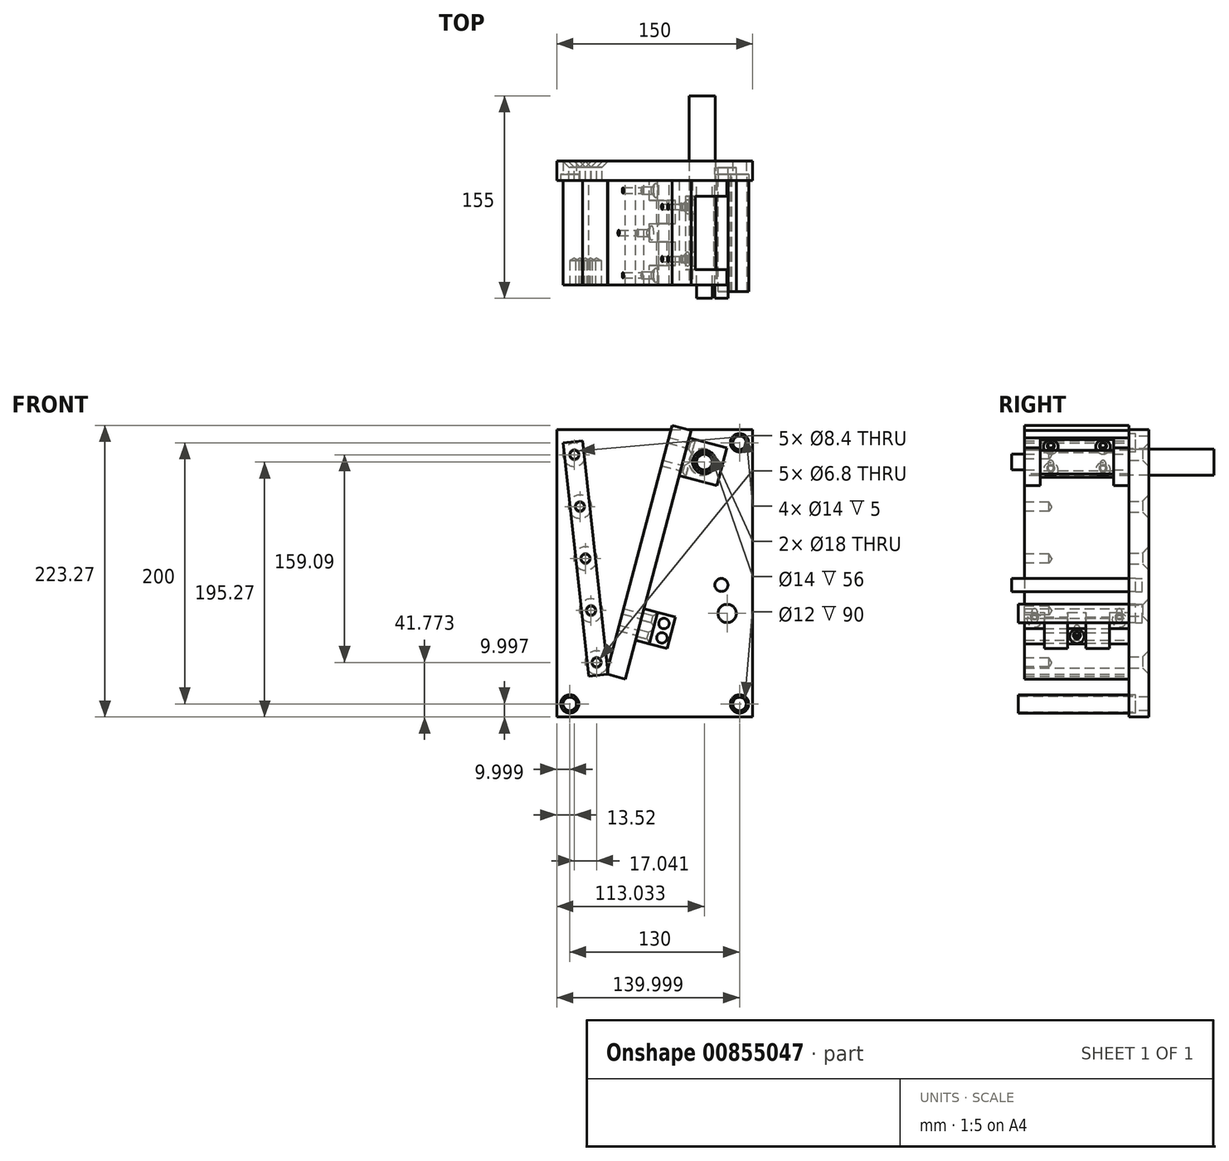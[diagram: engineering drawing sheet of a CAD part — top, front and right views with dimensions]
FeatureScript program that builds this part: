
annotation { "Feature Type Name" : "Feature", "Feature Type Description" : "" }
export const myFeature = defineFeature(function(context is Context, id is Id, definition is map)
    precondition{}
    {
        {
            var Q0;
            Q0=qCreatedBy(makeId("Front.planeOp"),FACE);
            var sketch = newSketch(context, id + "F0", { "sketchPlane" : qUnion([Q0])});
            skLineSegment(sketch, "E0", {"start": v(-17.27, 159) * mm, "end": v(0, 0) * mm});
            skLineSegment(sketch, "E1", {"start": v(0, 0) * mm, "end": v(42, 159) * mm});
            skLineSegment(sketch, "E2", {"start": v(42, 159) * mm, "end": v(142, 159) * mm});
            skLineSegment(sketch, "E3", {"start": v(142, 159) * mm, "end": v(123.08, 24.32) * mm});
            skLineSegment(sketch, "E4", {"start": v(123.08, 24.32) * mm, "end": v(218.62, 60.04) * mm});
            skLineSegment(sketch, "E5", {"start": v(124.98, 37.82) * mm, "end": v(164.87, 64.53) * mm});
            skLineSegment(sketch, "E6", {"start": v(-37.17, 28.68) * mm, "end": v(-37.17, -31.23) * mm, "construction": true});
            skLineSegment(sketch, "E7", {"start": v(-15.81, -31.23) * mm, "end": v(52.07, -31.23) * mm, "construction": true});
            skCircle(sketch, "E8", {"center": v(142, 159) * mm, "radius": 55 * mm});
            skCircle(sketch, "E9", {"center": v(142.6, 159) * mm, "radius": 8 * mm});
            skSolve(sketch);
        }
        {
            var Q0;
            Q0=qCreatedBy(makeId("Front.planeOp"),FACE);
            var sketch = newSketch(context, id + "F1", { "sketchPlane" : qUnion([Q0])});
            skLineSegment(sketch, "E10.bottom", {"start": v(-19.05, 175.35) * mm, "end": v(-33.96, 173.73) * mm});
            skLineSegment(sketch, "E10.top", {"start": v(-0.15, -3.66) * mm, "end": v(-14.52, -5.22) * mm});
            skLineSegment(sketch, "E10.left", {"start": v(-19.05, 175.35) * mm, "end": v(-0.15, 1.34) * mm});
            skLineSegment(sketch, "E10.right", {"start": v(-33.96, 173.73) * mm, "end": v(-14.52, -5.22) * mm});
            skLineSegment(sketch, "E11", {"start": v(-0.15, 1.34) * mm, "end": v(-0.15, -3.66) * mm});
            skLineSegment(sketch, "E12", {"start": v(0.35, 1.34) * mm, "end": v(0.35, -3.66) * mm, "construction": true});
            skSolve(sketch);
        }
        {
            var Q0;
            Q0 = qSketchRegion(id + "F1", true);
            extrude(context, id + "F2", {"entities" : qUnion([Q0]), "depth" : 80 * mm, "offsetDistance" : 25 * mm});
        }
        {
            var Q0;
            Q0=qCreatedBy(makeId("Front.planeOp"),FACE);
            var sketch = newSketch(context, id + "F3", { "sketchPlane" : qUnion([Q0])});
            skLineSegment(sketch, "E13.bottom", {"start": v(0.35, -3.66) * mm, "end": v(13.62, -7.16) * mm});
            skLineSegment(sketch, "E13.top", {"start": v(49.4, 187) * mm, "end": v(63.91, 183.17) * mm});
            skLineSegment(sketch, "E13.left", {"start": v(49.4, 187) * mm, "end": v(0.35, 1.34) * mm});
            skLineSegment(sketch, "E13.right", {"start": v(63.91, 183.17) * mm, "end": v(13.62, -7.16) * mm});
            skLineSegment(sketch, "E14", {"start": v(0.35, -3.66) * mm, "end": v(0.35, 1.34) * mm});
            skPoint(sketch, "E15", {"position": v(57.52, 159) * mm});
            skSolve(sketch);
        }
        {
            var Q0;
            Q0 = qSketchRegion(id + "F3", true);
            extrude(context, id + "F4", {"entities" : qUnion([Q0]), "depth" : 80 * mm, "offsetDistance" : 25 * mm});
        }
        {
            var Q0;
            Q0=qCreatedBy(makeId("Front.planeOp"),FACE);
            var sketch = newSketch(context, id + "F5", { "sketchPlane" : qUnion([Q0])});
            skLineSegment(sketch, "E16.bottom", {"start": v(21.44, 22.44) * mm, "end": v(45.61, 16.05) * mm});
            skLineSegment(sketch, "E16.top", {"start": v(27.83, 46.6) * mm, "end": v(52, 40.22) * mm});
            skLineSegment(sketch, "E16.left", {"start": v(21.44, 22.44) * mm, "end": v(27.83, 46.6) * mm});
            skLineSegment(sketch, "E16.right", {"start": v(45.61, 16.05) * mm, "end": v(52, 40.22) * mm});
            skCircle(sketch, "E17", {"center": v(43.14, 35.32) * mm, "radius": 4 * mm});
            skCircle(sketch, "E18", {"center": v(41.6, 24.32) * mm, "radius": 4 * mm});
            skLineSegment(sketch, "E19", {"start": v(60.52, 159) * mm, "end": v(41.6, 24.32) * mm, "construction": true});
            skLineSegment(sketch, "E20.0", {"start": v(42, 159) * mm, "end": v(142, 159) * mm, "construction": true});
            skSolve(sketch);
        }
        {
            var Q0;
            Q0 = qSketchRegion(id + "F5", true);
            extrude(context, id + "F6", {"entities" : qUnion([Q0]), "depth" : 80 * mm, "offsetDistance" : 25 * mm});
        }
        {
            var Q0;
            Q0=makeQuery(id+"F6.opExtrude","SWEPT_FACE",FACE,{"disambiguationData":[OSD([sQuery(id+"F5.wireOp",EDGE,"E16.right")])]});
            var sketch = newSketch(context, id + "F7", { "sketchPlane" : qUnion([Q0])});
            skLineSegment(sketch, "E21.bottom", {"start": v(-80, 52.17) * mm, "end": v(-65, 52.17) * mm});
            skLineSegment(sketch, "E21.top", {"start": v(-80, 27.17) * mm, "end": v(-65, 27.17) * mm});
            skLineSegment(sketch, "E21.left", {"start": v(-80, 52.17) * mm, "end": v(-80, 27.17) * mm});
            skLineSegment(sketch, "E21.right", {"start": v(-65, 52.17) * mm, "end": v(-65, 27.17) * mm});
            skLineSegment(sketch, "E22", {"start": v(-40, 52.17) * mm, "end": v(-40, 27.17) * mm, "construction": true});
            skLineSegment(sketch, "E23", {"start": v(-40, 27.17) * mm, "end": v(-40, 52.17) * mm, "construction": true});
            skLineSegment(sketch, "E24.MirrorCS", {"start": v(0, 52.17) * mm, "end": v(-15, 52.17) * mm});
            skLineSegment(sketch, "E25.MirrorCS", {"start": v(0, 52.17) * mm, "end": v(0, 27.17) * mm});
            skLineSegment(sketch, "E26.MirrorCS", {"start": v(-15, 52.17) * mm, "end": v(-15, 27.17) * mm});
            skLineSegment(sketch, "E27.MirrorCS", {"start": v(0, 27.17) * mm, "end": v(-15, 27.17) * mm});
            skLineSegment(sketch, "E28.bottom", {"start": v(-47, 27.17) * mm, "end": v(-33, 27.17) * mm});
            skLineSegment(sketch, "E28.top", {"start": v(-47, 52.17) * mm, "end": v(-33, 52.17) * mm});
            skLineSegment(sketch, "E28.left", {"start": v(-47, 27.17) * mm, "end": v(-47, 52.17) * mm});
            skLineSegment(sketch, "E28.right", {"start": v(-33, 27.17) * mm, "end": v(-33, 52.17) * mm});
            skSolve(sketch);
        }
        {
            var Q0;
            Q0=makeQuery(id+"F7.imprint","IMPRINT",FACE,{"disambiguationData":[TD([[makeQuery(id+"F7.imprint","IMPRINT",EDGE,{"derivedFrom":sQuery(id+"F7.wireOp",EDGE,"E21.bottom")}),-1.0]])]});
            var Q1;
            Q1=makeQuery(id+"F7.imprint","IMPRINT",FACE,{"disambiguationData":[TD([[makeQuery(id+"F7.imprint","IMPRINT",EDGE,{"derivedFrom":sQuery(id+"F7.wireOp",EDGE,"E28.bottom")}),1.0]])]});
            var Q2;
            Q2=makeQuery(id+"F7.imprint","IMPRINT",FACE,{"disambiguationData":[TD([[makeQuery(id+"F7.imprint","IMPRINT",EDGE,{"derivedFrom":sQuery(id+"F7.wireOp",EDGE,"E24.MirrorCS")}),-1.0]])]});
            extrude(context, id + "F8", {"entities" : qUnion([Q0, Q1, Q2]), "operationType" : NewBodyOperationType.REMOVE, "oppositeDirection" : true, "depth" : 14 * mm, "offsetDistance" : 25 * mm});
        }
        {
            var Q0;
            Q0=qCreatedBy(makeId("Front.planeOp"),FACE);
            var sketch = newSketch(context, id + "F9", { "sketchPlane" : qUnion([Q0])});
            skCircle(sketch, "E29.0", {"center": v(41.6, 24.32) * mm, "radius": 4 * mm, "construction": true});
            skCircle(sketch, "E30.0", {"center": v(43.14, 35.32) * mm, "radius": 4 * mm, "construction": true});
            skLineSegment(sketch, "E31", {"start": v(41.6, 24.32) * mm, "end": v(60.52, 159) * mm, "construction": true});
            skLineSegment(sketch, "E32.0", {"start": v(52, 40.22) * mm, "end": v(45.61, 16.05) * mm, "construction": true});
            skCircle(sketch, "E33", {"center": v(72.57, 159) * mm, "radius": 10 * mm});
            skCircle(sketch, "E34", {"center": v(74.07, 159) * mm, "radius": 6 * mm, "construction": true});
            skSolve(sketch);
        }
        {
            var Q0;
            Q0 = qSketchRegion(id + "F9", true);
            extrude(context, id + "F10", {"entities" : qUnion([Q0]), "oppositeDirection" : true, "depth" : 65 * mm, "offsetDistance" : 25 * mm});
        }
        {
            var Q0;
            Q0=makeQuery(id+"F9.imprint","IMPRINT",FACE,{"disambiguationData":[TD([[makeQuery(id+"F9.imprint","IMPRINT",EDGE,{"derivedFrom":sQuery(id+"F9.wireOp",EDGE,"E33")}),1.0]])]});
            var sketch = newSketch(context, id + "F11", { "sketchPlane" : qUnion([Q0])});
            skCircle(sketch, "E35", {"center": v(74.07, 159) * mm, "radius": 6 * mm});
            skSolve(sketch);
        }
        {
            var Q0;
            Q0 = qSketchRegion(id + "F11", true);
            extrude(context, id + "F12", {"entities" : qUnion([Q0]), "operationType" : NewBodyOperationType.ADD, "depth" : 90 * mm, "offsetDistance" : 25 * mm});
        }
        {
            var Q0;
            Q0=makeQuery(id+"F4.opExtrude","CAP_FACE",FACE,{"disambiguationData":[OSD([sQuery(id+"F3.wireOp",EDGE,"E13.bottom"),sQuery(id+"F3.wireOp",EDGE,"E13.top"),sQuery(id+"F3.wireOp",EDGE,"E13.left"),sQuery(id+"F3.wireOp",EDGE,"E13.right")])],"isStart":false});
            var sketch = newSketch(context, id + "F13", { "sketchPlane" : qUnion([Q0])});
            skLineSegment(sketch, "E36.bottom", {"start": v(54.77, 148.58) * mm, "end": v(83.78, 140.92) * mm});
            skLineSegment(sketch, "E36.top", {"start": v(62.44, 177.59) * mm, "end": v(91.44, 169.93) * mm});
            skLineSegment(sketch, "E36.left", {"start": v(54.77, 148.58) * mm, "end": v(62.44, 177.59) * mm});
            skLineSegment(sketch, "E36.right", {"start": v(83.78, 140.92) * mm, "end": v(91.44, 169.93) * mm});
            skCircle(sketch, "E37", {"center": v(74.07, 159) * mm, "radius": 9 * mm});
            skCircle(sketch, "E38.0", {"center": v(74.07, 159) * mm, "radius": 6 * mm, "construction": true});
            skLineSegment(sketch, "E39", {"start": v(87.6, 155.42) * mm, "end": v(58.6, 163.09) * mm, "construction": true});
            skSolve(sketch);
        }
        {
            var Q0;
            Q0 = qSketchRegion(id + "F13", true);
            extrude(context, id + "F14", {"entities" : qUnion([Q0]), "oppositeDirection" : true, "depth" : 80 * mm, "offsetDistance" : 25 * mm});
        }
        {
            var Q0;
            Q0=makeQuery(id+"F14.opExtrude","SWEPT_FACE",FACE,{"disambiguationData":[OSD([sQuery(id+"F13.wireOp",EDGE,"E36.right")])]});
            var sketch = newSketch(context, id + "F15", { "sketchPlane" : qUnion([Q0])});
            skLineSegment(sketch, "E40.bottom", {"start": v(-68, 187.65) * mm, "end": v(-12, 187.65) * mm});
            skLineSegment(sketch, "E40.top", {"start": v(-68, 157.65) * mm, "end": v(-12, 157.65) * mm});
            skLineSegment(sketch, "E40.left", {"start": v(-68, 187.65) * mm, "end": v(-68, 157.65) * mm});
            skLineSegment(sketch, "E40.right", {"start": v(-12, 187.65) * mm, "end": v(-12, 157.65) * mm});
            skSolve(sketch);
        }
        {
            var Q0;
            Q0 = qSketchRegion(id + "F15", true);
            extrude(context, id + "F16", {"entities" : qUnion([Q0]), "operationType" : NewBodyOperationType.REMOVE, "oppositeDirection" : true, "depth" : 25 * mm, "offsetDistance" : 25 * mm});
        }
        {
            var Q0;
            Q0=makeQuery(id+"F16.boolean.opBoolean","COPY",FACE,{"derivedFrom":makeQuery(id+"F16.opExtrude","SWEPT_FACE",FACE,{"disambiguationData":[OSD([sQuery(id+"F15.wireOp",EDGE,"E40.left")])]})});
            var sketch = newSketch(context, id + "F17", { "sketchPlane" : qUnion([Q0])});
            skCircle(sketch, "E41", {"center": v(-74.07, 159) * mm, "radius": 7 * mm});
            skCircle(sketch, "E42", {"center": v(-74.07, 159) * mm, "radius": 9 * mm});
            skCircle(sketch, "E43.0", {"center": v(-74.07, 159) * mm, "radius": 6 * mm});
            skSolve(sketch);
        }
        {
            var Q0;
            Q0 = qSketchRegion(id + "F17", true);
            extrude(context, id + "F18", {"entities" : qUnion([Q0]), "depth" : 56 * mm, "offsetDistance" : 25 * mm});
        }
        {
            var Q0;
            Q0=qCreatedBy(makeId("Front.planeOp"),FACE);
            var sketch = newSketch(context, id + "F19", { "sketchPlane" : qUnion([Q0])});
            skLineSegment(sketch, "E44", {"start": v(41.6, 24.32) * mm, "end": v(137.13, 60.04) * mm, "construction": true});
            skCircle(sketch, "E45.0", {"center": v(41.6, 24.32) * mm, "radius": 4 * mm});
            skLineSegment(sketch, "E46", {"start": v(61.5, 25.36) * mm, "end": v(57.29, 36.6) * mm});
            skLineSegment(sketch, "E47", {"start": v(57.29, 36.6) * mm, "end": v(33.87, 27.84) * mm});
            skLineSegment(sketch, "E48", {"start": v(33.87, 27.84) * mm, "end": v(38.07, 16.6) * mm});
            skLineSegment(sketch, "E49", {"start": v(38.07, 16.6) * mm, "end": v(61.5, 25.36) * mm});
            skSolve(sketch);
        }
        {
            var Q0;
            Q0=qCreatedBy(makeId("Front.planeOp"),FACE);
            var sketch = newSketch(context, id + "F20", { "sketchPlane" : qUnion([Q0])});
            skLineSegment(sketch, "E50", {"start": v(43.14, 35.32) * mm, "end": v(83.03, 62.03) * mm, "construction": true});
            skCircle(sketch, "E51.0", {"center": v(43.14, 35.32) * mm, "radius": 4 * mm, "construction": true});
            skCircle(sketch, "E52.0", {"center": v(41.6, 24.32) * mm, "radius": 4 * mm, "construction": true});
            skCircle(sketch, "E53", {"center": v(91.6, 43.02) * mm, "radius": 7 * mm});
            skSolve(sketch);
        }
        {
            var Q0;
            Q0 = qSketchRegion(id + "F20", true);
            extrude(context, id + "F21", {"entities" : qUnion([Q0]), "depth" : 85 * mm, "offsetDistance" : 25 * mm, "hasSecondDirection" : true, "secondDirectionOppositeDirection" : true, "secondDirectionDepth" : 10 * mm});
        }
        {
            var Q0;
            Q0=qCreatedBy(makeId("Front.planeOp"),FACE);
            var sketch = newSketch(context, id + "F22", { "sketchPlane" : qUnion([Q0])});
            skCircle(sketch, "E54", {"center": v(87.18, 64.8) * mm, "radius": 5 * mm});
            skSolve(sketch);
        }
        {
            var Q0;
            Q0 = qSketchRegion(id + "F22", true);
            extrude(context, id + "F23", {"entities" : qUnion([Q0]), "depth" : 90 * mm, "offsetDistance" : 25 * mm, "hasSecondDirection" : true, "secondDirectionOppositeDirection" : true, "secondDirectionDepth" : 10 * mm});
        }
        {
            var Q0;
            Q0=makeQuery(id+"F8.boolean.opBoolean","COPY",FACE,{"derivedFrom":makeQuery(id+"F8.opExtrude","CAP_FACE",FACE,{"disambiguationData":[OSD([sQuery(id+"F7.wireOp",EDGE,"E24.MirrorCS"),sQuery(id+"F7.wireOp",EDGE,"E25.MirrorCS"),sQuery(id+"F7.wireOp",EDGE,"E26.MirrorCS"),sQuery(id+"F7.wireOp",EDGE,"E27.MirrorCS")])],"isStart":false})});
            var sketch = newSketch(context, id + "F24", { "sketchPlane" : qUnion([Q0])});
            skPoint(sketch, "E55", {"position": v(-72.5, 46.17) * mm});
            skPoint(sketch, "E56", {"position": v(-40, 33.17) * mm});
            skPoint(sketch, "E57", {"position": v(-7.5, 46.17) * mm});
            skPoint(sketch, "E58.0", {"position": v(-40, 52.17) * mm});
            skPoint(sketch, "E59.0", {"position": v(-7.5, 52.17) * mm});
            skPoint(sketch, "E60.0", {"position": v(-72.5, 52.17) * mm});
            skSolve(sketch);
        }
        {
            var Q0;
            Q0=sQuery(id+"F24.wireOp",VERTEX,"E57");
            var Q1;
            Q1=sQuery(id+"F24.wireOp",VERTEX,"E56");
            var Q2;
            Q2=sQuery(id+"F24.wireOp",VERTEX,"E55");
            var Q3;
            Q3=makeQuery(id+"F6.opExtrude","SWEPT_BODY",BODY,{"disambiguationData":[OSD([sQuery(id+"F5.wireOp",EDGE,"E16.bottom"),sQuery(id+"F5.wireOp",EDGE,"E16.top"),sQuery(id+"F5.wireOp",EDGE,"E16.left"),sQuery(id+"F5.wireOp",EDGE,"E16.right"),sQuery(id+"F5.wireOp",EDGE,"E17"),sQuery(id+"F5.wireOp",EDGE,"E18")])]});
            hole(context, id + "F25", {"style" : HoleStyle.C_SINK, "endStyle" : HoleEndStyle.THROUGH, "standardTappedOrClearance" : lookupTablePath({ "fit" : "Normal", "standard" : "ISO", "size" : "M5", "type" : "Clearance" }), "standardBlindInLast" : lookupTablePath({ "fit" : "Normal", "standard" : "ISO", "size" : "M5", "type" : "Clearance" }), "holeDiameter" : 5.5 * mm, "cSinkDiameter" : 11.2 * mm, "cSinkAngle" : 90 * degree, "majorDiameter" : 6 * mm, "isTappedThrough" : true, "tappedDepth" : 8 * mm, "tapClearance" : 3, "startFromSketch" : true, "locations" : qUnion([Q0, Q1, Q2]), "scope" : qUnion([Q3])});
        }
        {
            var Q0;
            Q0=qCreatedBy(makeId("Front.planeOp"),FACE);
            var sketch = newSketch(context, id + "F26", { "sketchPlane" : qUnion([Q0])});
            skLineSegment(sketch, "E61.bottom", {"start": v(-38.96, -36.27) * mm, "end": v(111.04, -36.27) * mm});
            skLineSegment(sketch, "E61.top", {"start": v(-38.96, 183.73) * mm, "end": v(111.04, 183.73) * mm});
            skLineSegment(sketch, "E61.left", {"start": v(-38.96, -36.27) * mm, "end": v(-38.96, 183.73) * mm});
            skLineSegment(sketch, "E61.right", {"start": v(111.04, -36.27) * mm, "end": v(111.04, 183.73) * mm});
            skCircle(sketch, "E62.0", {"center": v(74.07, 159) * mm, "radius": 6 * mm, "construction": true});
            skCircle(sketch, "E63", {"center": v(-28.96, -26.27) * mm, "radius": 5.15 * mm});
            skCircle(sketch, "E64", {"center": v(101.04, -26.27) * mm, "radius": 5.15 * mm});
            skCircle(sketch, "E65", {"center": v(101.04, 173.73) * mm, "radius": 5.15 * mm});
            skCircle(sketch, "E66.0", {"center": v(72.57, 159) * mm, "radius": 10 * mm, "construction": true});
            skCircle(sketch, "E67", {"center": v(72.57, 159) * mm, "radius": 10.25 * mm});
            skSolve(sketch);
        }
        {
            var Q0;
            Q0 = qSketchRegion(id + "F26", true);
            extrude(context, id + "F27", {"entities" : qUnion([Q0]), "oppositeDirection" : true, "depth" : 15 * mm, "offsetDistance" : 25 * mm});
        }
        {
            var Q0;
            Q0=makeQuery(id+"F2.opExtrude","CAP_FACE",FACE,{"disambiguationData":[OSD([sQuery(id+"F1.wireOp",EDGE,"E10.bottom"),sQuery(id+"F1.wireOp",EDGE,"E10.top"),sQuery(id+"F1.wireOp",EDGE,"E10.left"),sQuery(id+"F1.wireOp",EDGE,"E10.right"),sQuery(id+"F1.wireOp",EDGE,"E11")])],"isStart":false});
            var sketch = newSketch(context, id + "F28", { "sketchPlane" : qUnion([Q0])});
            skLineSegment(sketch, "E68", {"start": v(-26.5, 174.54) * mm, "end": v(-7.33, -4.44) * mm, "construction": true});
            skPoint(sketch, "E69", {"position": v(-25.44, 164.6) * mm});
            skPoint(sketch, "E70", {"position": v(-21.18, 124.82) * mm});
            skPoint(sketch, "E71", {"position": v(-16.92, 85.05) * mm});
            skPoint(sketch, "E72", {"position": v(-8.4, 5.5) * mm});
            skPoint(sketch, "E73", {"position": v(-12.66, 45.28) * mm});
            skSolve(sketch);
        }
        {
            var Q0;
            Q0=sQuery(id+"F28.wireOp",VERTEX,"E69");
            var Q1;
            Q1=sQuery(id+"F28.wireOp",VERTEX,"E70");
            var Q2;
            Q2=sQuery(id+"F28.wireOp",VERTEX,"E71");
            var Q3;
            Q3=sQuery(id+"F28.wireOp",VERTEX,"E73");
            var Q4;
            Q4=sQuery(id+"F28.wireOp",VERTEX,"E72");
            var Q5;
            Q5=makeQuery(id+"F2.opExtrude","SWEPT_BODY",BODY,{"disambiguationData":[OSD([sQuery(id+"F1.wireOp",EDGE,"E10.bottom"),sQuery(id+"F1.wireOp",EDGE,"E10.top"),sQuery(id+"F1.wireOp",EDGE,"E10.left"),sQuery(id+"F1.wireOp",EDGE,"E10.right"),sQuery(id+"F1.wireOp",EDGE,"E11")])]});
            hole(context, id + "F29", {"style" : HoleStyle.SIMPLE, "endStyle" : HoleEndStyle.BLIND, "standardTappedOrClearance" : lookupTablePath({ "standard" : "ISO", "engagement" : "75%", "pitch" : "1.25 mm", "size" : "M8", "type" : "Tapped" }), "standardBlindInLast" : lookupTablePath({ "standard" : "ISO", "fit" : "Normal", "engagement" : "75%", "pitch" : "1.25 mm", "size" : "M8", "type" : "Clearance & tapped" }), "holeDiameter" : 6.8 * mm, "majorDiameter" : 8 * mm, "showTappedDepth" : true, "holeDepth" : 18.75 * mm, "isTappedThrough" : true, "tappedDepth" : 15 * mm, "tapClearance" : 3, "startFromSketch" : true, "locations" : qUnion([Q0, Q1, Q2, Q3, Q4]), "scope" : qUnion([Q5])});
        }
        {
            var Q0;
            Q0=makeQuery(id+"F27.opExtrude","CAP_FACE",FACE,{"disambiguationData":[OSD([sQuery(id+"F26.wireOp",EDGE,"E61.bottom"),sQuery(id+"F26.wireOp",EDGE,"E61.top"),sQuery(id+"F26.wireOp",EDGE,"E61.left"),sQuery(id+"F26.wireOp",EDGE,"E61.right"),sQuery(id+"F26.wireOp",EDGE,"E63"),sQuery(id+"F26.wireOp",EDGE,"E64"),sQuery(id+"F26.wireOp",EDGE,"E65"),sQuery(id+"F26.wireOp",EDGE,"E67")])],"isStart":false});
            var sketch = newSketch(context, id + "F30", { "sketchPlane" : qUnion([Q0])});
            skPoint(sketch, "E74.0", {"position": v(25.44, 164.6) * mm});
            skPoint(sketch, "E75.0", {"position": v(21.18, 124.82) * mm});
            skPoint(sketch, "E76.0", {"position": v(16.92, 85.05) * mm});
            skPoint(sketch, "E77.0", {"position": v(12.66, 45.28) * mm});
            skPoint(sketch, "E78.0", {"position": v(8.4, 5.5) * mm});
            skSolve(sketch);
        }
        {
            var Q0;
            Q0=sQuery(id+"F30.wireOp",VERTEX,"E74.0");
            var Q1;
            Q1=sQuery(id+"F30.wireOp",VERTEX,"E75.0");
            var Q2;
            Q2=sQuery(id+"F30.wireOp",VERTEX,"E76.0");
            var Q3;
            Q3=sQuery(id+"F30.wireOp",VERTEX,"E77.0");
            var Q4;
            Q4=sQuery(id+"F30.wireOp",VERTEX,"E78.0");
            var Q5;
            Q5=makeQuery(id+"F27.opExtrude","SWEPT_BODY",BODY,{"disambiguationData":[OSD([sQuery(id+"F26.wireOp",EDGE,"E61.bottom"),sQuery(id+"F26.wireOp",EDGE,"E61.top"),sQuery(id+"F26.wireOp",EDGE,"E61.left"),sQuery(id+"F26.wireOp",EDGE,"E61.right"),sQuery(id+"F26.wireOp",EDGE,"E63"),sQuery(id+"F26.wireOp",EDGE,"E64"),sQuery(id+"F26.wireOp",EDGE,"E65"),sQuery(id+"F26.wireOp",EDGE,"E67")])]});
            hole(context, id + "F31", {"style" : HoleStyle.C_SINK, "endStyle" : HoleEndStyle.THROUGH, "standardTappedOrClearance" : lookupTablePath({ "fit" : "Close", "standard" : "ISO", "size" : "M8", "type" : "Clearance" }), "standardBlindInLast" : lookupTablePath({ "fit" : "Close", "standard" : "ISO", "engagement" : "75%", "pitch" : "1.25 mm", "size" : "M8", "type" : "Clearance & tapped" }), "holeDiameter" : 8.4 * mm, "cSinkDiameter" : 17.92 * mm, "cSinkAngle" : 90 * degree, "majorDiameter" : 8 * mm, "isTappedThrough" : true, "tappedDepth" : 8 * mm, "tapClearance" : 3, "startFromSketch" : true, "locations" : qUnion([Q0, Q1, Q2, Q3, Q4]), "scope" : qUnion([Q5])});
        }
        {
            var Q0;
            Q0=makeQuery(id+"F2.opExtrude","CAP_FACE",FACE,{"disambiguationData":[OSD([sQuery(id+"F1.wireOp",EDGE,"E10.bottom"),sQuery(id+"F1.wireOp",EDGE,"E10.top"),sQuery(id+"F1.wireOp",EDGE,"E10.left"),sQuery(id+"F1.wireOp",EDGE,"E10.right"),sQuery(id+"F1.wireOp",EDGE,"E11")])],"isStart":false});
            var Q1;
            Q1=makeQuery(id+"F2.opExtrude","CAP_FACE",FACE,{"disambiguationData":[OSD([sQuery(id+"F1.wireOp",EDGE,"E10.bottom"),sQuery(id+"F1.wireOp",EDGE,"E10.top"),sQuery(id+"F1.wireOp",EDGE,"E10.left"),sQuery(id+"F1.wireOp",EDGE,"E10.right"),sQuery(id+"F1.wireOp",EDGE,"E11")])],"isStart":true});
            cPlane(context, id + "F32", {"entities" : qUnion([Q0, Q1]), "cplaneType" : CPlaneType.MID_PLANE, "offset" : 25 * mm, "width" : 150 * mm, "height" : 150 * mm});
        }
        {
            var Q0;
            Q0=makeQuery(id+"F16.boolean.opBoolean","COPY",FACE,{"derivedFrom":makeQuery(id+"F16.opExtrude","CAP_FACE",FACE,{"disambiguationData":[OSD([sQuery(id+"F15.wireOp",EDGE,"E40.bottom"),sQuery(id+"F15.wireOp",EDGE,"E40.top"),sQuery(id+"F15.wireOp",EDGE,"E40.left"),sQuery(id+"F15.wireOp",EDGE,"E40.right")])],"isStart":false})});
            var sketch = newSketch(context, id + "F33", { "sketchPlane" : qUnion([Q0])});
            skLineSegment(sketch, "E79.bottom", {"start": v(-60, 181.65) * mm, "end": v(-20, 181.65) * mm, "construction": true});
            skLineSegment(sketch, "E79.top", {"start": v(-60, 163.65) * mm, "end": v(-20, 163.65) * mm, "construction": true});
            skLineSegment(sketch, "E79.left", {"start": v(-60, 181.65) * mm, "end": v(-60, 163.65) * mm, "construction": true});
            skLineSegment(sketch, "E79.right", {"start": v(-20, 181.65) * mm, "end": v(-20, 163.65) * mm, "construction": true});
            skPoint(sketch, "E80", {"position": v(-60, 181.65) * mm});
            skPoint(sketch, "E81", {"position": v(-20, 181.65) * mm});
            skPoint(sketch, "E82", {"position": v(-20, 163.65) * mm});
            skPoint(sketch, "E83", {"position": v(-60, 163.65) * mm});
            skSolve(sketch);
        }
        {
            var Q0;
            Q0=sQuery(id+"F33.wireOp",VERTEX,"E80");
            var Q1;
            Q1=sQuery(id+"F33.wireOp",VERTEX,"E83");
            var Q2;
            Q2=sQuery(id+"F33.wireOp",VERTEX,"E82");
            var Q3;
            Q3=sQuery(id+"F33.wireOp",VERTEX,"E81");
            var Q4;
            Q4=makeQuery(id+"F14.opExtrude","SWEPT_BODY",BODY,{"disambiguationData":[OSD([sQuery(id+"F13.wireOp",EDGE,"E36.bottom"),sQuery(id+"F13.wireOp",EDGE,"E36.top"),sQuery(id+"F13.wireOp",EDGE,"E36.left"),sQuery(id+"F13.wireOp",EDGE,"E36.right"),sQuery(id+"F13.wireOp",EDGE,"E37")])]});
            hole(context, id + "F34", {"style" : HoleStyle.C_SINK, "endStyle" : HoleEndStyle.THROUGH, "standardTappedOrClearance" : lookupTablePath({ "fit" : "Normal", "standard" : "ISO", "size" : "M5", "type" : "Clearance" }), "standardBlindInLast" : lookupTablePath({ "fit" : "Normal", "standard" : "ISO", "engagement" : "75%", "pitch" : "0.8 mm", "size" : "M5", "type" : "Clearance & tapped" }), "holeDiameter" : 5.5 * mm, "cSinkDiameter" : 11.2 * mm, "cSinkAngle" : 90 * degree, "majorDiameter" : 5 * mm, "isTappedThrough" : true, "tappedDepth" : 8 * mm, "tapClearance" : 3, "startFromSketch" : true, "locations" : qUnion([Q0, Q1, Q2, Q3]), "scope" : qUnion([Q4])});
        }
        {
            var Q0;
            Q0=makeQuery(id+"F4.opExtrude","SWEPT_FACE",FACE,{"disambiguationData":[OSD([sQuery(id+"F3.wireOp",EDGE,"E13.right")])]});
            var sketch = newSketch(context, id + "F35", { "sketchPlane" : qUnion([Q0])});
            skPoint(sketch, "E84.0", {"position": v(-60, 181.65) * mm});
            skPoint(sketch, "E85.0", {"position": v(-60, 163.65) * mm});
            skPoint(sketch, "E86.0", {"position": v(-20, 181.65) * mm});
            skPoint(sketch, "E87.0", {"position": v(-20, 163.65) * mm});
            skPoint(sketch, "E88.0", {"position": v(-72.5, 46.17) * mm});
            skPoint(sketch, "E89.0", {"position": v(-40, 33.17) * mm});
            skPoint(sketch, "E90.0", {"position": v(-7.5, 46.17) * mm});
            skSolve(sketch);
        }
        {
            var Q0;
            Q0=sQuery(id+"F35.wireOp",VERTEX,"E84.0");
            var Q1;
            Q1=sQuery(id+"F35.wireOp",VERTEX,"E85.0");
            var Q2;
            Q2=sQuery(id+"F35.wireOp",VERTEX,"E87.0");
            var Q3;
            Q3=sQuery(id+"F35.wireOp",VERTEX,"E86.0");
            var Q4;
            Q4=sQuery(id+"F35.wireOp",VERTEX,"E89.0");
            var Q5;
            Q5=sQuery(id+"F35.wireOp",VERTEX,"E90.0");
            var Q6;
            Q6=sQuery(id+"F35.wireOp",VERTEX,"E88.0");
            var Q7;
            Q7=makeQuery(id+"F4.opExtrude","SWEPT_BODY",BODY,{"disambiguationData":[OSD([sQuery(id+"F3.wireOp",EDGE,"E13.bottom"),sQuery(id+"F3.wireOp",EDGE,"E13.top"),sQuery(id+"F3.wireOp",EDGE,"E13.left"),sQuery(id+"F3.wireOp",EDGE,"E13.right"),sQuery(id+"F3.wireOp",EDGE,"E14")])]});
            hole(context, id + "F36", {"style" : HoleStyle.SIMPLE, "endStyle" : HoleEndStyle.THROUGH, "standardTappedOrClearance" : lookupTablePath({ "standard" : "ISO", "engagement" : "75%", "pitch" : "0.8 mm", "size" : "M5", "type" : "Tapped" }), "standardBlindInLast" : lookupTablePath({ "standard" : "ISO", "fit" : "Normal", "engagement" : "75%", "pitch" : "0.8 mm", "size" : "M5", "type" : "Clearance & tapped" }), "holeDiameter" : 4.2 * mm, "majorDiameter" : 5 * mm, "showTappedDepth" : true, "isTappedThrough" : true, "tappedDepth" : 8 * mm, "tapClearance" : 3, "startFromSketch" : true, "locations" : qUnion([Q0, Q1, Q2, Q3, Q4, Q5, Q6]), "scope" : qUnion([Q7])});
        }
        {
            var Q0;
            Q0=makeQuery(id+"F27.opExtrude","CAP_FACE",FACE,{"disambiguationData":[OSD([sQuery(id+"F26.wireOp",EDGE,"E61.bottom"),sQuery(id+"F26.wireOp",EDGE,"E61.top"),sQuery(id+"F26.wireOp",EDGE,"E61.left"),sQuery(id+"F26.wireOp",EDGE,"E61.right"),sQuery(id+"F26.wireOp",EDGE,"E63"),sQuery(id+"F26.wireOp",EDGE,"E64"),sQuery(id+"F26.wireOp",EDGE,"E65"),sQuery(id+"F26.wireOp",EDGE,"E67")])],"isStart":true});
            var sketch = newSketch(context, id + "F37", { "sketchPlane" : qUnion([Q0])});
            skCircle(sketch, "E91", {"center": v(101.04, 173.73) * mm, "radius": 7 * mm});
            skCircle(sketch, "E92", {"center": v(101.04, -26.27) * mm, "radius": 7 * mm});
            skCircle(sketch, "E93", {"center": v(-28.96, -26.27) * mm, "radius": 7 * mm});
            skCircle(sketch, "E94.0", {"center": v(87.18, 64.8) * mm, "radius": 5 * mm});
            skCircle(sketch, "E95.0", {"center": v(91.6, 43.02) * mm, "radius": 7 * mm});
            skSolve(sketch);
        }
        {
            var Q0;
            Q0 = qSketchRegion(id + "F37", true);
            extrude(context, id + "F38", {"entities" : qUnion([Q0]), "operationType" : NewBodyOperationType.REMOVE, "oppositeDirection" : true, "depth" : 5 * mm, "offsetDistance" : 25 * mm});
        }
        {
            var Q0;
            Q0=makeQuery(id+"F38.boolean.opBoolean","COPY",FACE,{"derivedFrom":makeQuery(id+"F38.opExtrude","CAP_FACE",FACE,{"disambiguationData":[OSD([sQuery(id+"F37.wireOp",EDGE,"E92")])],"isStart":false})});
            var sketch = newSketch(context, id + "F39", { "sketchPlane" : qUnion([Q0])});
            skCircle(sketch, "E96.0", {"center": v(101.04, -26.27) * mm, "radius": 7 * mm});
            skCircle(sketch, "E97.0", {"center": v(-28.96, -26.27) * mm, "radius": 7 * mm});
            skCircle(sketch, "E98.0", {"center": v(101.04, 173.73) * mm, "radius": 7 * mm});
            skCircle(sketch, "E99.0", {"center": v(101.04, 173.73) * mm, "radius": 6 * mm});
            skCircle(sketch, "E100.0", {"center": v(101.04, -26.27) * mm, "radius": 6 * mm});
            skCircle(sketch, "E101.0", {"center": v(-28.96, -26.27) * mm, "radius": 6 * mm});
            skSolve(sketch);
        }
        {
            var Q0;
            Q0 = qSketchRegion(id + "F39", true);
            extrude(context, id + "F40", {"entities" : qUnion([Q0]), "depth" : 90 * mm, "offsetDistance" : 25 * mm});
        }
        {
            var Q0;
            Q0=makeQuery(id+"F40.opExtrude","SWEPT_BODY",BODY,{"disambiguationData":[OSD([sQuery(id+"F39.wireOp",EDGE,"E97.0"),sQuery(id+"F39.wireOp",EDGE,"E101.0")])]});
            var Q1;
            Q1=makeQuery(id+"F40.opExtrude","SWEPT_BODY",BODY,{"disambiguationData":[OSD([sQuery(id+"F39.wireOp",EDGE,"E98.0"),sQuery(id+"F39.wireOp",EDGE,"E99.0")])]});
            deleteBodies(context, id + "F41", {"entities" : qUnion([Q0, Q1])});
        }
        {
            var Q0;
            Q0=makeQuery(id+"F27.opExtrude","CAP_FACE",FACE,{"disambiguationData":[OSD([sQuery(id+"F26.wireOp",EDGE,"E61.bottom"),sQuery(id+"F26.wireOp",EDGE,"E61.top"),sQuery(id+"F26.wireOp",EDGE,"E61.left"),sQuery(id+"F26.wireOp",EDGE,"E61.right"),sQuery(id+"F26.wireOp",EDGE,"E63"),sQuery(id+"F26.wireOp",EDGE,"E64"),sQuery(id+"F26.wireOp",EDGE,"E65"),sQuery(id+"F26.wireOp",EDGE,"E67")])],"isStart":true});
            var sketch = newSketch(context, id + "F42", { "sketchPlane" : qUnion([Q0])});
            skCircle(sketch, "E102.0", {"center": v(43.14, 35.32) * mm, "radius": 4 * mm});
            skSolve(sketch);
        }
        {
            var Q0;
            Q0 = qSketchRegion(id + "F42", true);
            extrude(context, id + "F43", {"entities" : qUnion([Q0]), "depth" : 80 * mm, "offsetDistance" : 25 * mm});
        }
    });
